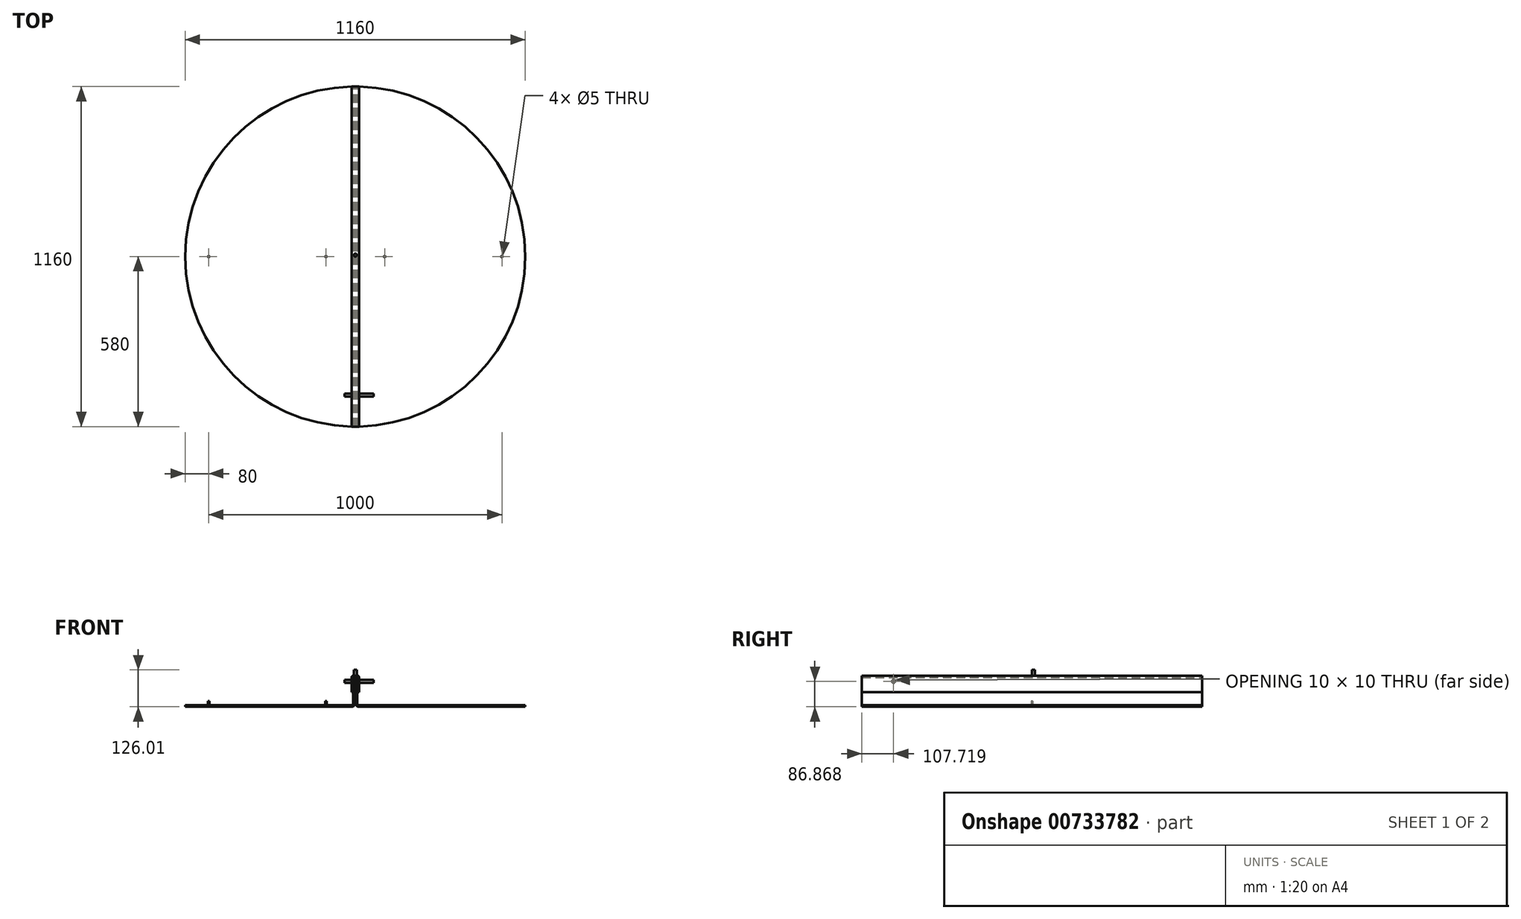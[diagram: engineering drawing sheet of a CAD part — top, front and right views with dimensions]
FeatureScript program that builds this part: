
annotation { "Feature Type Name" : "Feature", "Feature Type Description" : "" }
export const myFeature = defineFeature(function(context is Context, id is Id, definition is map)
    precondition{}
    {
        {
            var Q0;
            Q0=qCreatedBy(makeId("Top.planeOp"),FACE);
            var sketch = newSketch(context, id + "F0", { "sketchPlane" : qUnion([Q0])});
            skArc(sketch, "E0", {"start": v(0, 580) * mm, "mid": v(-580, 0) * mm, "end": v(0, -580) * mm});
            skLineSegment(sketch, "E1", {"start": v(0, 0) * mm, "end": v(0, 580) * mm});
            skLineSegment(sketch, "E2", {"start": v(0, 0) * mm, "end": v(0, -580) * mm});
            skLineSegment(sketch, "E3", {"start": v(0, 0) * mm, "end": v(-100, 0) * mm});
            skLineSegment(sketch, "E4", {"start": v(-100, 0) * mm, "end": v(-500, 0) * mm});
            skCircle(sketch, "E5", {"center": v(-100, 0) * mm, "radius": 2.5 * mm});
            skCircle(sketch, "E6", {"center": v(-500, 0) * mm, "radius": 2.5 * mm});
            skSolve(sketch);
        }
        {
            var Q0;
            Q0=qSketchRegion(id+"F0",true);
            extrude(context, id + "F1", {"entities" : qUnion([Q0]), "depth" : 5 * mm, "offsetDistance" : 25 * mm});
        }
        {
            var Q0;
            Q0=qCreatedBy(makeId("Front.planeOp"),FACE);
            var sketch = newSketch(context, id + "F2", { "sketchPlane" : qUnion([Q0])});
            skLineSegment(sketch, "E7.bottom", {"start": v(0, 0) * mm, "end": v(-7, 0) * mm});
            skLineSegment(sketch, "E7.left", {"start": v(0, 0) * mm, "end": v(0, 100) * mm, "construction": true});
            skLineSegment(sketch, "E8.bottom", {"start": v(-7, 0) * mm, "end": v(-2, 0) * mm});
            skLineSegment(sketch, "E8.top", {"start": v(-7, 100) * mm, "end": v(-2, 100) * mm});
            skLineSegment(sketch, "E8.left", {"start": v(-7, 0) * mm, "end": v(-7, 1.34) * mm});
            skLineSegment(sketch, "E8.right", {"start": v(-2, 10) * mm, "end": v(-2, 100) * mm});
            skLineSegment(sketch, "E9.bottom", {"start": v(-7, 0) * mm, "end": v(-12, 0) * mm});
            skLineSegment(sketch, "E9.right", {"start": v(-12, 0) * mm, "end": v(-12, 5) * mm});
            skArc(sketch, "E10", {"start": v(-12, 5) * mm, "mid": v(-8.46, 6.46) * mm, "end": v(-7, 10) * mm});
            skArc(sketch, "E11", {"start": v(-12, 0) * mm, "mid": v(-4.93, 2.93) * mm, "end": v(-2, 10) * mm});
            skLineSegment(sketch, "E12", {"start": v(-7, 10) * mm, "end": v(-2, 10) * mm});
            skLineSegment(sketch, "E13.trimOffspring", {"start": v(-7, 10) * mm, "end": v(-7, 100) * mm});
            skSolve(sketch);
        }
        {
            var Q0;
            Q0=qSketchRegion(id+"F2",true);
            extrude(context, id + "F3", {"entities" : qUnion([Q0]), "operationType" : NewBodyOperationType.ADD, "endBound" : BoundingType.SYMMETRIC, "depth" : 1160 * mm, "offsetDistance" : 25 * mm});
        }
        {
            var Q0;
            Q0=makeQuery(id+"F1.opExtrude","SWEPT_FACE",FACE,{"disambiguationData":[OSD([sQuery(id+"F0.wireOp",EDGE,"E1"),sQuery(id+"F0.wireOp",EDGE,"E2")])]});
            extrude(context, id + "F4", {"entities" : qUnion([Q0]), "operationType" : NewBodyOperationType.REMOVE, "oppositeDirection" : true, "depth" : 12 * mm, "offsetDistance" : 25 * mm});
        }
        {
            var Q0;
            Q0=makeQuery(id+"F2.imprint","IMPRINT",FACE,{"disambiguationData":[TD([[makeQuery(id+"F2.imprint","IMPRINT",EDGE,{"derivedFrom":sQuery(id+"F2.wireOp",EDGE,"E10")}),-1.0]])]});
            var Q1;
            Q1=makeQuery(id+"F2.imprint","IMPRINT",FACE,{"disambiguationData":[TD([[makeQuery(id+"F2.imprint","IMPRINT",EDGE,{"derivedFrom":sQuery(id+"F2.wireOp",EDGE,"E8.top")}),-1.0]])]});
            extrude(context, id + "F5", {"entities" : qUnion([Q0, Q1]), "operationType" : NewBodyOperationType.ADD, "endBound" : BoundingType.SYMMETRIC, "depth" : 1160 * mm, "offsetDistance" : 25 * mm});
        }
        {
            var Q0;
            Q0=makeQuery(id+"F1.opExtrude","SWEPT_BODY",BODY,{"disambiguationData":[OSD([sQuery(id+"F0.wireOp",EDGE,"E0"),sQuery(id+"F0.wireOp",EDGE,"E1"),sQuery(id+"F0.wireOp",EDGE,"E2")])]});
            var Q1;
            Q1=qCreatedBy(makeId("Right.planeOp"),FACE);
            mirror(context, id + "F6", {"entities" : qUnion([Q0]), "mirrorPlane" : qUnion([Q1])});
        }
        {
            var Q0;
            Q0=qCreatedBy(makeId("Front.planeOp"),FACE);
            var sketch = newSketch(context, id + "F7", { "sketchPlane" : qUnion([Q0])});
            skArc(sketch, "E14", {"start": v(8, 100) * mm, "mid": v(7.7, 100.71) * mm, "end": v(7, 101) * mm});
            skLineSegment(sketch, "E15", {"start": v(7, 101) * mm, "end": v(0, 101) * mm});
            skLineSegment(sketch, "E16", {"start": v(8, 100) * mm, "end": v(8, 50) * mm});
            skLineSegment(sketch, "E17.0", {"start": v(7, 106) * mm, "end": v(0, 106) * mm});
            skArc(sketch, "E17.1", {"start": v(13, 100) * mm, "mid": v(11.24, 104.25) * mm, "end": v(7, 106) * mm});
            skLineSegment(sketch, "E17.2", {"start": v(13, 100) * mm, "end": v(13, 50) * mm});
            skPoint(sketch, "E18.startSnap0", {"position": v(0, 101) * mm});
            skPoint(sketch, "E19.orphan", {"position": v(0, 100.07) * mm});
            skLineSegment(sketch, "E20", {"start": v(8, 50) * mm, "end": v(13, 50) * mm});
            skArc(sketch, "E21.MirrorCS", {"start": v(-8, 100) * mm, "mid": v(-7.7, 100.71) * mm, "end": v(-7, 101) * mm});
            skLineSegment(sketch, "E22.MirrorCS", {"start": v(-7, 101) * mm, "end": v(0, 101) * mm});
            skLineSegment(sketch, "E23.MirrorCS", {"start": v(-13, 100) * mm, "end": v(-13, 50) * mm});
            skLineSegment(sketch, "E24.MirrorCS", {"start": v(-7, 106) * mm, "end": v(0, 106) * mm});
            skLineSegment(sketch, "E25.MirrorCS", {"start": v(-8, 50) * mm, "end": v(-13, 50) * mm});
            skArc(sketch, "E26.MirrorCS", {"start": v(-13, 100) * mm, "mid": v(-11.24, 104.25) * mm, "end": v(-7, 106) * mm});
            skLineSegment(sketch, "E27.MirrorCS", {"start": v(-8, 100) * mm, "end": v(-8, 50) * mm});
            skSolve(sketch);
        }
        {
            var Q0;
            Q0=qSketchRegion(id+"F7",true);
            extrude(context, id + "F8", {"entities" : qUnion([Q0]), "endBound" : BoundingType.SYMMETRIC, "depth" : 1160 * mm, "offsetDistance" : 25 * mm});
        }
        {
            var Q0;
            Q0=makeQuery(id+"F0.imprint","IMPRINT",FACE,{"disambiguationData":[TD([[makeQuery(id+"F0.imprint","IMPRINT",EDGE,{"derivedFrom":sQuery(id+"F0.wireOp",EDGE,"E6")}),1.0]])]});
            extrude(context, id + "F9", {"entities" : qUnion([Q0]), "depth" : 20 * mm, "offsetDistance" : 25 * mm});
        }
        {
            var Q0;
            {var subQ0=sQuery(id+"F0.wireOp",EDGE,"E4");var subQ1=sQuery(id+"F0.wireOp",EDGE,"E3");var subQ2=makeQuery(id+"F0.imprint","INTERSECT",VERTEX,{"derivedFrom":[subQ1,subQ0]});Q0=makeQuery(id+"F0.imprint","IMPRINT",FACE,{"disambiguationData":[TD([[makeQuery(id+"F0.imprint","IMPRINT",EDGE,{"disambiguationData":[TD([[subQ2,1.0]])],"derivedFrom":subQ1}),-1.0]])]});}
            var Q1;
            {var subQ0=sQuery(id+"F0.wireOp",EDGE,"E4");var subQ1=sQuery(id+"F0.wireOp",EDGE,"E3");var subQ2=makeQuery(id+"F0.imprint","INTERSECT",VERTEX,{"derivedFrom":[subQ1,subQ0]});Q1=makeQuery(id+"F0.imprint","IMPRINT",FACE,{"disambiguationData":[TD([[makeQuery(id+"F0.imprint","IMPRINT",EDGE,{"disambiguationData":[TD([[subQ2,1.0]])],"derivedFrom":subQ1}),1.0]])]});}
            extrude(context, id + "F10", {"entities" : qUnion([Q0, Q1]), "depth" : 20 * mm, "offsetDistance" : 25 * mm});
        }
        {
            var Q0;
            Q0=makeQuery(id+"F8.opExtrude","SWEPT_FACE",FACE,{"disambiguationData":[OSD([sQuery(id+"F7.wireOp",EDGE,"E17.0"),sQuery(id+"F7.wireOp",EDGE,"E24.MirrorCS")])]});
            var sketch = newSketch(context, id + "F11", { "sketchPlane" : qUnion([Q0])});
            skCircle(sketch, "E28", {"center": v(0, 5.1) * mm, "radius": 5 * mm});
            skSolve(sketch);
        }
        {
            var Q0;
            Q0=makeQuery(id+"F11.imprint","IMPRINT",FACE,{"disambiguationData":[TD([[makeQuery(id+"F11.imprint","IMPRINT",EDGE,{"derivedFrom":sQuery(id+"F11.wireOp",EDGE,"E28")}),1.0]])]});
            extrude(context, id + "F12", {"entities" : qUnion([Q0]), "operationType" : NewBodyOperationType.ADD, "depth" : 20 * mm, "offsetDistance" : 25 * mm});
        }
        {
            var Q0;
            Q0=makeQuery(id+"F8.opExtrude","SWEPT_FACE",FACE,{"disambiguationData":[OSD([sQuery(id+"F7.wireOp",EDGE,"E17.2")])]});
            var sketch = newSketch(context, id + "F13", { "sketchPlane" : qUnion([Q0])});
            skCircle(sketch, "E29", {"center": v(-472.28, 86.87) * mm, "radius": 5 * mm});
            skSolve(sketch);
        }
        {
            var Q0;
            Q0=makeQuery(id+"F13.imprint","IMPRINT",FACE,{"disambiguationData":[TD([[makeQuery(id+"F13.imprint","IMPRINT",EDGE,{"derivedFrom":sQuery(id+"F13.wireOp",EDGE,"E29")}),1.0]])]});
            extrude(context, id + "F14", {"entities" : qUnion([Q0]), "operationType" : NewBodyOperationType.ADD, "endBound" : BoundingType.SYMMETRIC, "depth" : 100 * mm, "offsetDistance" : 25 * mm});
        }
    });
